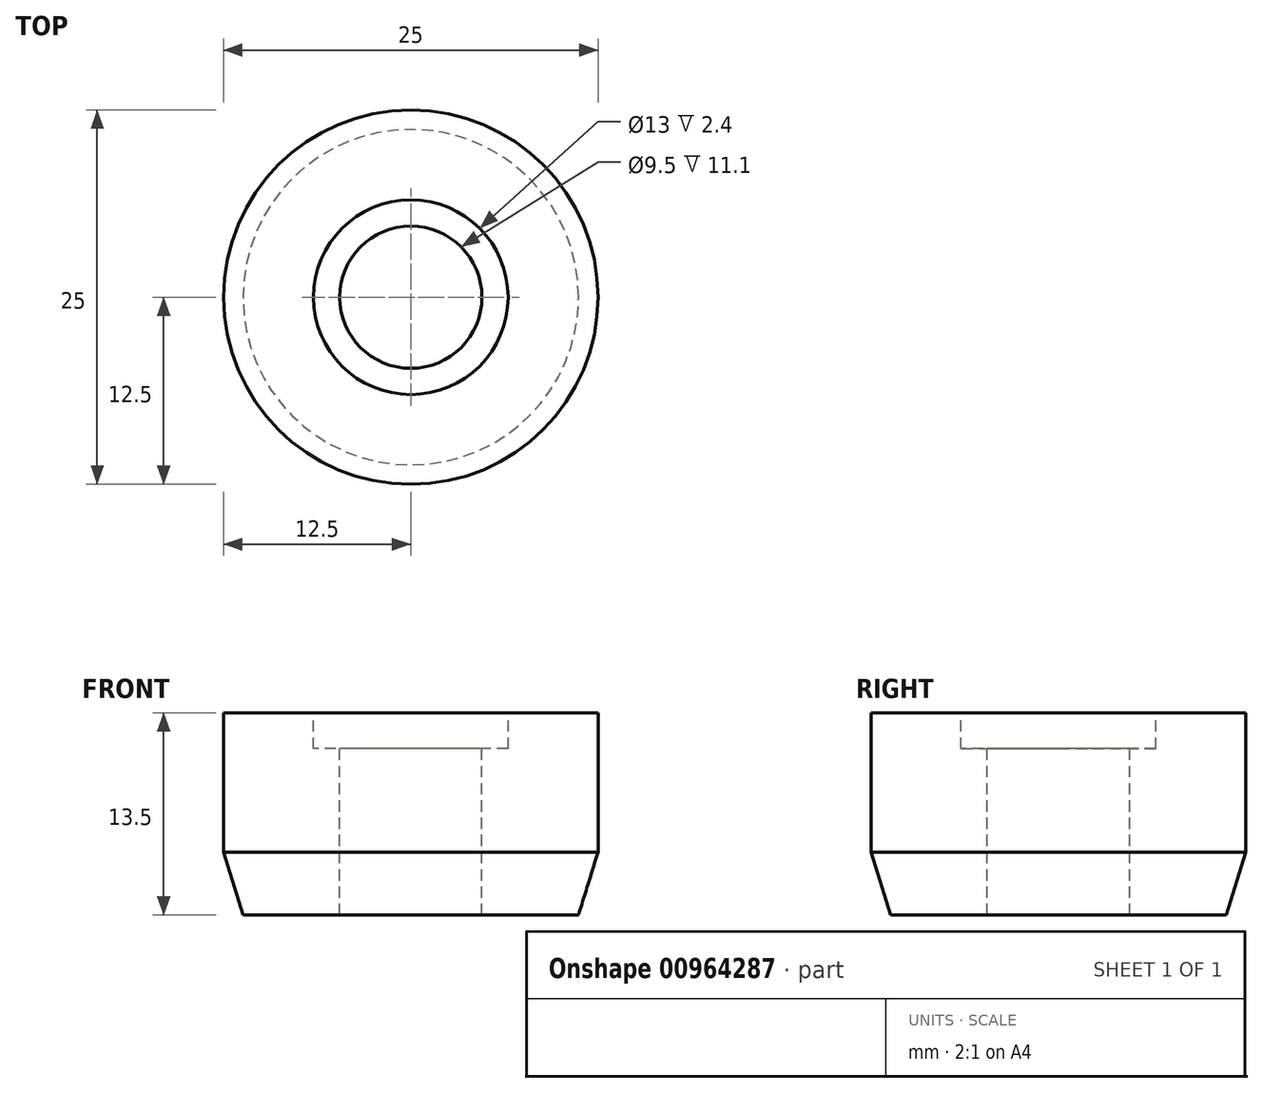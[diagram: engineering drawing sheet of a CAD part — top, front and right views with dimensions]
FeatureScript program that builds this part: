
annotation { "Feature Type Name" : "Feature", "Feature Type Description" : "" }
export const myFeature = defineFeature(function(context is Context, id is Id, definition is map)
    precondition{}
    {
        {
            var Q0;
            Q0=qCreatedBy(makeId("Front.planeOp"),FACE);
            var sketch = newSketch(context, id + "F0", { "sketchPlane" : qUnion([Q0])});
            skLineSegment(sketch, "E0", {"start": v(0, 0) * mm, "end": v(0, -4.86) * mm, "construction": true});
            skLineSegment(sketch, "E1", {"start": v(6.5, 0) * mm, "end": v(12.5, 0) * mm});
            skLineSegment(sketch, "E2", {"start": v(12.5, 0) * mm, "end": v(12.5, -9.3) * mm});
            skLineSegment(sketch, "E3", {"start": v(12.5, -9.3) * mm, "end": v(11.2, -13.5) * mm});
            skLineSegment(sketch, "E4", {"start": v(11.2, -13.5) * mm, "end": v(4.75, -13.5) * mm});
            skLineSegment(sketch, "E5", {"start": v(4.75, -13.5) * mm, "end": v(4.75, -2.4) * mm});
            skLineSegment(sketch, "E6", {"start": v(4.75, -2.4) * mm, "end": v(6.5, -2.4) * mm});
            skLineSegment(sketch, "E7", {"start": v(6.5, 0) * mm, "end": v(6.5, -2.4) * mm});
            skSolve(sketch);
        }
        {
            var Q0;
            Q0 = qSketchRegion(id + "F0", true);
            var Q1;
            Q1=sQuery(id+"F0.wireOp",EDGE,"E0");
            revolve(context, id + "F1", {"surfaceOperationType" : NewSurfaceOperationType.NEW, "entities" : qUnion([Q0]), "axis" : qUnion([Q1]), "revolveType" : RevolveType.FULL});
        }
    });
